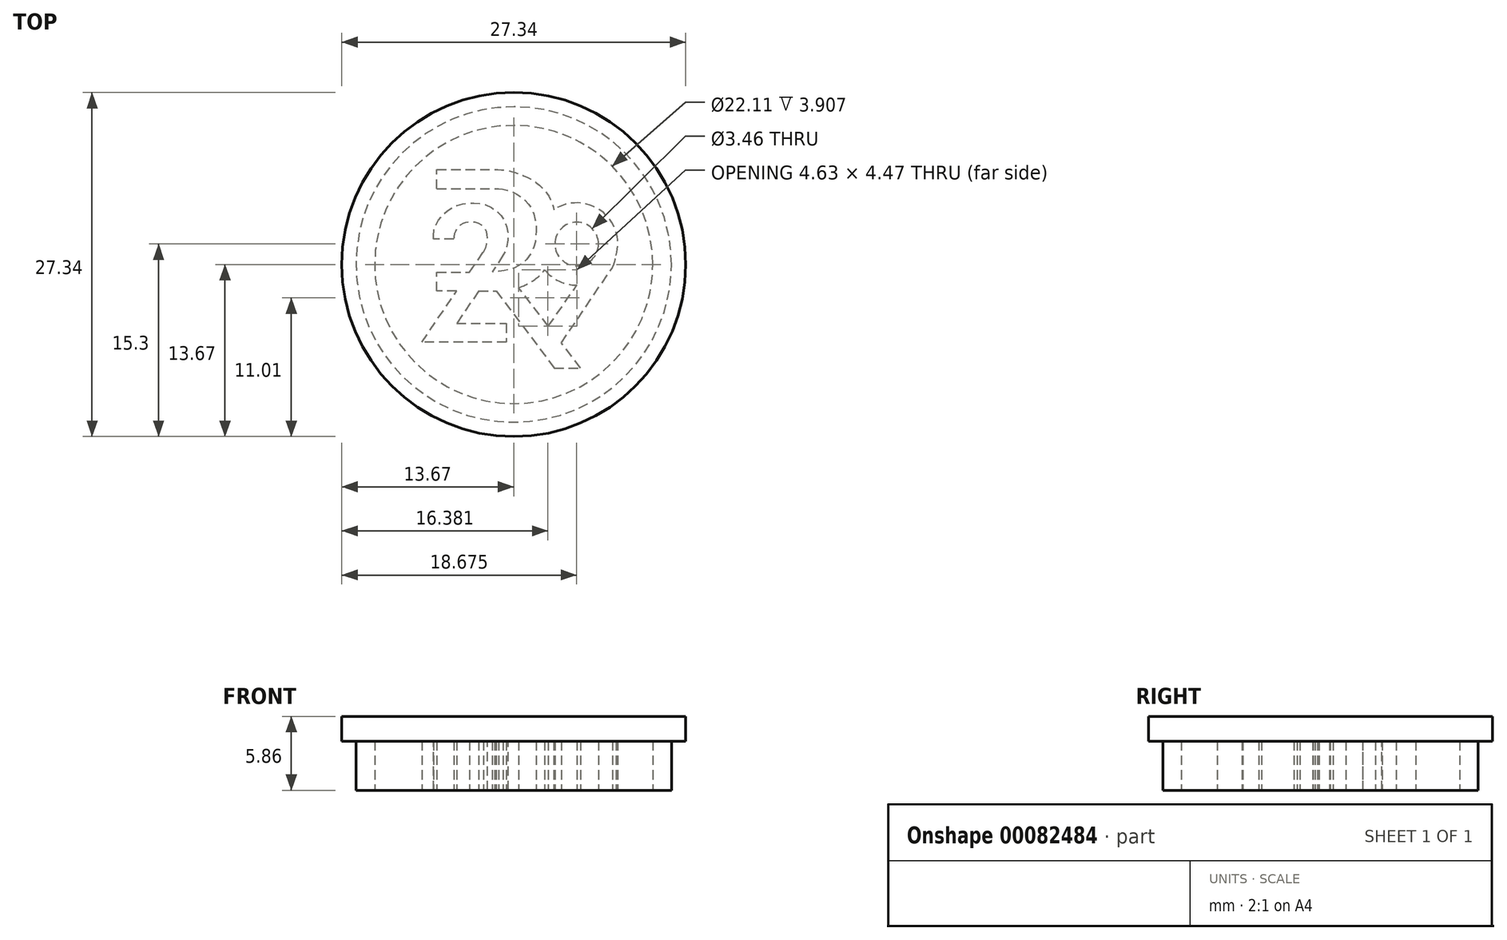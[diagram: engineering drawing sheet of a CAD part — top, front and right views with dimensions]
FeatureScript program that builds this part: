
annotation { "Feature Type Name" : "Feature", "Feature Type Description" : "" }
export const myFeature = defineFeature(function(context is Context, id is Id, definition is map)
    precondition{}
    {
        {
            var Q0;
            Q0=qCreatedBy(makeId("Top.planeOp"),FACE);
            var sketch = newSketch(context, id + "F0", { "sketchPlane" : qUnion([Q0])});
            skLineSegment(sketch, "E0", {"start": v(-55.19, -55.19) * mm, "end": v(55.19, 55.19) * mm, "construction": true});
            skLineSegment(sketch, "E1.bottom", {"start": v(50.8, -50.8) * mm, "end": v(-50.8, -50.8) * mm});
            skLineSegment(sketch, "E1.top", {"start": v(50.8, 50.8) * mm, "end": v(-50.8, 50.8) * mm});
            skLineSegment(sketch, "E1.left", {"start": v(50.8, -50.8) * mm, "end": v(50.8, 50.8) * mm});
            skLineSegment(sketch, "E1.right", {"start": v(-50.8, -50.8) * mm, "end": v(-50.8, 50.8) * mm});
            skPoint(sketch, "E1.middle", {"position": v(0, 0) * mm});
            skCircle(sketch, "E2", {"center": v(0, 0) * mm, "radius": 40.74 * mm});
            skCircle(sketch, "E3", {"center": v(0, 0) * mm, "radius": 35.94 * mm});
            skLineSegment(sketch, "E4", {"start": v(-19.9, 19.53) * mm, "end": v(-19.9, 24.58) * mm});
            skLineSegment(sketch, "E5", {"start": v(-19.9, 24.58) * mm, "end": v(-4.96, 24.58) * mm});
            skFitSpline(sketch, "E6", {"points": [v(-4.96, 24.58) * mm, v(-1.56, 24.26) * mm, v(1.68, 23.29) * mm, v(4.75, 21.85) * mm, v(8.06, 19.08) * mm, v(9.73, 16.2) * mm, v(10.39, 14.14) * mm], "startDerivative": vector(20.2, -1) * mm, "endDerivative": vector(4.16, -14.8) * mm});
            skCircle(sketch, "E7", {"center": v(16.27, 5.3) * mm, "radius": 5.63 * mm});
            skArc(sketch, "E8", {"start": v(8.01, -1.38) * mm, "mid": v(11.73, -4.3) * mm, "end": v(16.34, -5.32) * mm});
            skLineSegment(sketch, "E9", {"start": v(-9.07, -6.9) * mm, "end": v(-4.5, -6.9) * mm});
            skLineSegment(sketch, "E10", {"start": v(-4.5, -6.9) * mm, "end": v(10.47, -26.72) * mm});
            skLineSegment(sketch, "E11", {"start": v(10.47, -26.72) * mm, "end": v(17.3, -26.72) * mm});
            skLineSegment(sketch, "E12", {"start": v(17.3, -26.72) * mm, "end": v(12.3, -20.26) * mm});
            skLineSegment(sketch, "E13", {"start": v(12.3, -20.28) * mm, "end": v(25.48, -0.81) * mm});
            skFitSpline(sketch, "E14", {"points": [v(25.48, -0.81) * mm, v(25.99, 0.37) * mm, v(26.47, 2.33) * mm], "startDerivative": vector(1.18, 2.5) * mm, "endDerivative": vector(0.8, 3.75) * mm});
            skLineSegment(sketch, "E15", {"start": v(8.95, -15.92) * mm, "end": v(16.34, -5.32) * mm});
            skLineSegment(sketch, "E16.trimOffspring", {"start": v(8.95, -15.92) * mm, "end": v(1.29, -6.02) * mm});
            skFitSpline(sketch, "E17", {"points": [v(1.29, -6.02) * mm, v(3.16, -5.2) * mm, v(5.14, -4.07) * mm, v(6.77, -2.77) * mm, v(8.01, -1.38) * mm], "startDerivative": vector(7.44, 3.1) * mm, "endDerivative": vector(5.02, 5.98) * mm});
            skLineSegment(sketch, "E18", {"start": v(-9.07, -6.9) * mm, "end": v(-14.78, -15.25) * mm});
            skLineSegment(sketch, "E19", {"start": v(-14.78, -15.25) * mm, "end": v(-1.9, -15.25) * mm});
            skLineSegment(sketch, "E20", {"start": v(-1.9, -15.25) * mm, "end": v(-1.9, -20.07) * mm});
            skLineSegment(sketch, "E21", {"start": v(-1.9, -20.07) * mm, "end": v(-23.76, -20.07) * mm});
            skLineSegment(sketch, "E22", {"start": v(-23.76, -20.07) * mm, "end": v(-14.75, -6.9) * mm});
            skLineSegment(sketch, "E23", {"start": v(-14.75, -6.9) * mm, "end": v(-19.9, -6.9) * mm});
            skLineSegment(sketch, "E24", {"start": v(-19.9, -6.9) * mm, "end": v(-19.9, -1.98) * mm});
            skLineSegment(sketch, "E25", {"start": v(-19.9, -1.98) * mm, "end": v(-11.4, -1.98) * mm});
            skLineSegment(sketch, "E26", {"start": v(-11.4, -1.98) * mm, "end": v(-7.85, 3.22) * mm});
            skFitSpline(sketch, "E27", {"points": [v(-7.85, 3.22) * mm, v(-7.1, 4.75) * mm, v(-6.82, 7.07) * mm, v(-7.24, 8.91) * mm, v(-8.64, 10.4) * mm, v(-11.06, 10.98) * mm, v(-13.1, 10.6) * mm, v(-14.51, 9.43) * mm, v(-15.28, 8.03) * mm, v(-15.47, 6.58) * mm], "startDerivative": vector(7.97, 13.46) * mm, "endDerivative": vector(-0.85, -14.95) * mm});
            skLineSegment(sketch, "E28", {"start": v(-15.47, 6.58) * mm, "end": v(-20.75, 6.58) * mm});
            skFitSpline(sketch, "E29", {"points": [v(-20.75, 6.58) * mm, v(-20.75, 7.84) * mm, v(-20.46, 9.5) * mm, v(-19.16, 11.86) * mm, v(-16.8, 14.16) * mm, v(-14.88, 15.18) * mm, v(-12.6, 15.78) * mm, v(-10.18, 15.87) * mm, v(-7.66, 15.56) * mm, v(-4.9, 14.14) * mm, v(-2.98, 12.26) * mm, v(-1.72, 9.41) * mm, v(-1.53, 6.01) * mm, v(-2.2, 3.45) * mm, v(-2.7, 2.47) * mm], "startDerivative": vector(-0.6, 23.73) * mm, "endDerivative": vector(-10.54, -17.64) * mm});
            skLineSegment(sketch, "E30", {"start": v(-2.7, 2.47) * mm, "end": v(-5.5, -1.87) * mm});
            skLineSegment(sketch, "E31", {"start": v(-19.9, 19.53) * mm, "end": v(-3.93, 19.53) * mm});
            skFitSpline(sketch, "E32", {"points": [v(-3.93, 19.53) * mm, v(-2.42, 19.4) * mm, v(-0.43, 18.79) * mm, v(1.48, 17.72) * mm, v(3.11, 16.37) * mm, v(4.56, 14.54) * mm, v(5.43, 12.06) * mm, v(5.8, 9.46) * mm, v(5.68, 6.7) * mm, v(5.25, 4.69) * mm, v(3.18, 1.12) * mm, v(0, -0.97) * mm, v(-2.6, -1.62) * mm, v(-5.5, -1.87) * mm], "startDerivative": vector(24.68, -1.1) * mm, "endDerivative": vector(-36.13, -2.37) * mm});
            skArc(sketch, "E33.trimOffspring", {"start": v(26.47, 2.33) * mm, "mid": v(22.56, 13.86) * mm, "end": v(10.39, 14.14) * mm});
            skSolve(sketch);
        }
        {
            var Q0;
            Q0=makeQuery(id+"F0.imprint","IMPRINT",FACE,{"disambiguationData":[TD([[makeQuery(id+"F0.imprint","IMPRINT",EDGE,{"derivedFrom":sQuery(id+"F0.wireOp",EDGE,"E2")}),1.0]])]});
            var Q1;
            Q1=makeQuery(id+"F0.imprint","IMPRINT",FACE,{"disambiguationData":[TD([[makeQuery(id+"F0.imprint","IMPRINT",EDGE,{"derivedFrom":sQuery(id+"F0.wireOp",EDGE,"E4")}),-1.0]])]});
            extrude(context, id + "F1", {"entities" : qUnion([Q0, Q1]), "depth" : 12.7 * mm});
        }
        {
            var Q0;
            Q0=makeQuery(id+"F1.opExtrude","CAP_FACE",FACE,{"disambiguationData":[OSD([sQuery(id+"F0.wireOp",EDGE,"E2"),sQuery(id+"F0.wireOp",EDGE,"E3")])],"isStart":false});
            var sketch = newSketch(context, id + "F2", { "sketchPlane" : qUnion([Q0])});
            skCircle(sketch, "E34", {"center": v(0, 0) * mm, "radius": 44.45 * mm});
            skSolve(sketch);
        }
        {
            var Q0;
            Q0=makeQuery(id+"F2.imprint","IMPRINT",FACE,{"disambiguationData":[TD([[makeQuery(id+"F2.imprint","IMPRINT",EDGE,{"derivedFrom":sQuery(id+"F2.wireOp",EDGE,"E34")}),1.0]])]});
            var Q1;
            Q1=makeQuery(id+"F2.imprint","IMPRINT",FACE,{"disambiguationData":[TD([[makeQuery(id+"F2.imprint","IMPRINT",EDGE,{"derivedFrom":makeQuery(id+"F1.opExtrude","CAP_EDGE",EDGE,{"disambiguationData":[OSD([sQuery(id+"F0.wireOp",EDGE,"E2")])],"isStart":false})}),1.0]])]});
            var Q2;
            Q2=makeQuery(id+"F2.imprint","IMPRINT",FACE,{"disambiguationData":[TD([[makeQuery(id+"F2.imprint","IMPRINT",EDGE,{"derivedFrom":makeQuery(id+"F1.opExtrude","CAP_EDGE",EDGE,{"disambiguationData":[OSD([sQuery(id+"F0.wireOp",EDGE,"E3")])],"isStart":false})}),1.0]])]});
            extrude(context, id + "F3", {"entities" : qUnion([Q0, Q1, Q2]), "depth" : 6.35 * mm});
        }
        {
            var Q0;
            Q0=makeQuery(id+"F1.opExtrude","SWEPT_BODY",BODY,{"disambiguationData":[OSD([sQuery(id+"F0.wireOp",EDGE,"E2"),sQuery(id+"F0.wireOp",EDGE,"E3")])]});
            var Q1;
            Q1=makeQuery(id+"F1.opExtrude","SWEPT_BODY",BODY,{"disambiguationData":[OSD([sQuery(id+"F0.wireOp",EDGE,"E4"),sQuery(id+"F0.wireOp",EDGE,"E5"),sQuery(id+"F0.wireOp",EDGE,"E6"),sQuery(id+"F0.wireOp",EDGE,"E7"),sQuery(id+"F0.wireOp",EDGE,"E8"),sQuery(id+"F0.wireOp",EDGE,"E9"),sQuery(id+"F0.wireOp",EDGE,"E10"),sQuery(id+"F0.wireOp",EDGE,"E11"),sQuery(id+"F0.wireOp",EDGE,"E12"),sQuery(id+"F0.wireOp",EDGE,"E13"),sQuery(id+"F0.wireOp",EDGE,"E14"),sQuery(id+"F0.wireOp",EDGE,"E15"),sQuery(id+"F0.wireOp",EDGE,"E16.trimOffspring"),sQuery(id+"F0.wireOp",EDGE,"E17"),sQuery(id+"F0.wireOp",EDGE,"E18"),sQuery(id+"F0.wireOp",EDGE,"E19"),sQuery(id+"F0.wireOp",EDGE,"E20"),sQuery(id+"F0.wireOp",EDGE,"E21"),sQuery(id+"F0.wireOp",EDGE,"E22"),sQuery(id+"F0.wireOp",EDGE,"E23"),sQuery(id+"F0.wireOp",EDGE,"E24"),sQuery(id+"F0.wireOp",EDGE,"E25"),sQuery(id+"F0.wireOp",EDGE,"E26"),sQuery(id+"F0.wireOp",EDGE,"E27"),sQuery(id+"F0.wireOp",EDGE,"E28"),sQuery(id+"F0.wireOp",EDGE,"E29"),sQuery(id+"F0.wireOp",EDGE,"E30"),sQuery(id+"F0.wireOp",EDGE,"E31"),sQuery(id+"F0.wireOp",EDGE,"E32"),sQuery(id+"F0.wireOp",EDGE,"E33.trimOffspring")])]});
            var Q2;
            Q2=makeQuery(id+"F3.opExtrude","SWEPT_BODY",BODY,{"disambiguationData":[OSD([sQuery(id+"F2.wireOp",EDGE,"E34")])]});
            var Q3;
            Q3=qCreatedBy(makeId("Origin.pointOp"),VERTEX);
            transform(context, id + "F4", {"entities" : qUnion([Q0, Q1, Q2]), "transformType" : TransformType.SCALE_UNIFORMLY, "scale" : 0.3, "scalePoint" : qUnion([Q3]), "makeCopy" : false});
        }
    });
